# Revit family: MC10LED
name_source: partatom
category: Lighting Fixtures
revit_build: Autodesk Revit MEP 2012 (Build: 20110916_2132(x64)
units: mm (PartAtom-declared; Revit-internal decimal feet)

## types (2) — shared parameters
Apparent Load = 40 VA
Color Filter = 16777215
Default Elevation = 48.000"
Description = 10 Inch High Lumen LED Cylinder
Dimming Lamp Color Temperature Shift = <None>
Emit Shape Visible in Rendering = No
Emit from Circle Diameter = 8.000"
Glass = Hubbell - White Glass
Is 120V = Yes
Is 277V = No
Lamp = LED Lamp
Load Classification = Lighting
Manufacturer = Prescolite
Manufacturer Fax = 866-898-0131
Model = MC10LED
Photometric Web File = generic
Product Documentation Link = http://cdn.prescolite.com
Product Page URL = http://www.prescolite.com
Tilt Angle = -90.00°
URL = http://www.prescolite.com
Voltage = 120 V
Wattage Comments = 40W

## per-type parameters (varying)
| type | Backbox | Housing |
| MC10LED - 26 Inch Housing | Hubbell - Matt Black | 23.500" |
| MC10LED - 30 Inch Housing | Hubbell - Matt White | 26.750" |

## geometry (parser evidence)
native form markers: Blend x2, Sweep x1
no freeform markers — native parametric forms only
